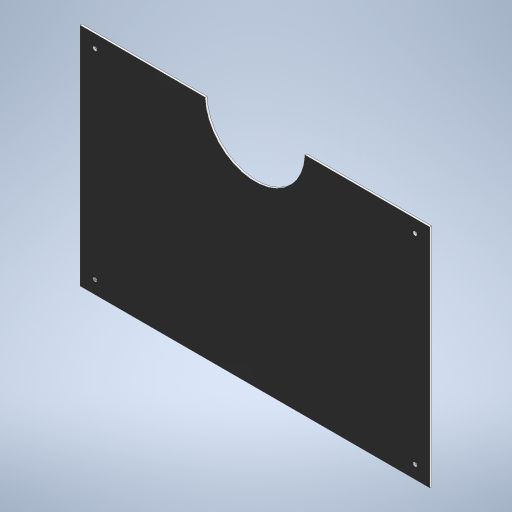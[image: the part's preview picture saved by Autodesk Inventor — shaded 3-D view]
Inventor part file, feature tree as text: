
AUTODESK INVENTOR PART (.ipt)
format: ipt  version: 2023 (Build 270158000, 158)  size: 232,448 bytes
history: native  units: mm
features: sketch x2, extrude x1, hole x1
ambient origin geometry x8: Origin, YZ Plane, XZ Plane, XY Plane, X Axis, Y Axis, Z Axis, Center Point
bodies: Solid1 (feature_tree)
feature tree (4):
  extrude  "Extrusion1"  Depth=350.0mm
  hole  "Hole1"  [1 undecoded]
  sketch  "Sketch1"  dims[d0=542.0mm d1=350.0mm]
  sketch  "Sketch2"  dims[d2=3.0mm d3=0.0mm d4=23.0mm d6=6.5mm d7=6.0mm d8=4.0mm d9=2.0mm d10=90.0deg d11=8.0mm d12=20.594885mm d13=20.0mm d14=350.0mm d15=542.0mm d16=20.0mm d18=310.0mm d19=20.0mm d21=496.0mm d24=155.0mm d25=353.0mm]
note: 1 required parameter value undecoded (feature->parameter linkage not recoverable at this tier; creation-order binding heuristic only, values carry confidence <= 0.55)
